# Revit family: ASH_Waste_Multiproduct_BIM_GB_S8735;S8737;S8803;S8808
name_source: partatom
category: Plumbing Fixtures
revit_build: Autodesk Revit MEP 2014 (Build: 20130308_1515(x64)
units: mm (PartAtom-declared; Revit-internal decimal feet)

## types (4) — shared parameters
Accessories = www.idealspec.co.uk
AreaUnits = millimeters
Assembly Code = C1030200
AssetType = Fixed
Brand = Armitage Shanks
BrassMtl = ISI_IdealStandard_Washbasin_Brass_Render
ChromeMtl = ISI_IdealStandard_Washbasin_Chrome_Render
Color = Chrome
ConnectionType = Plumbing
DrainSize = 32 mm
DurationUnit = year
ECA = No
ExpectedLife = 30
Finish = Chrome
Help = www.idealspec.co.uk/contact-us.html
IfcExportAs = IfcWasteTerminalType
IfcExportType = WASTETRAP
InstallationInstructions = www.idealspec.co.uk/resources.html
LinearUnits = millimeters
ManufacturerURL = www.idealspec.co.uk
Material = Brass
NBSDescription = Wastes for wash basins
NBSReference = 45-35-70/372
NettWeight = 0.62 Kg
NominalHeight = 62 mm
NominalWidth = 62 mm
RubberMtl = ISI_IdealStandard_Washbasin_Rubber_Render
Shape = Sculptured
Space = Internal
URL = www.idealspec.co.uk
Uniclass2015Description = Waste traps
Uniclass2015Reference = Pr_65_52_25_98
Uniclass2015Version = Products v1.1
Version = 1
VolumeUnits = Litres
WRAS = No
WarrantyDescription = Manufacturers Warranty
WarrantyDurationParts = 5
WarrantyDurationUnit = year
WashHandBasinMounting = Other
WashHandBasinType = Hand Rinse
WaterEfficientProduct = No
zero-valued in all types: CWFU, Cost, Default Elevation, HWFU, WFU

## per-type parameters (varying)
| type | BIMObjectName | ClickPlug | Description | Features | Model | ModelNumber | ModelReference | Name | NominalDepth | NominalLength | ProductInformation | RubberPlug | Size |
| S8735AA - Waste 1¼" Anti Theft - Bolt & Chain - Slotted - Brass | ISI_IdealStandard_Waste_1¼"AntiTheftBolt&ChainSlotted_S8735AA | No | Waste 1¼" Anti Theft - Bolt & Chain - Slotted - Brass | 1¼" Anti Theft - Bolt & Chain - Slotted - Brass | S8735AA | S8735AA | Waste 1¼" Anti Theft - Bolt & Chain - Slotted - Brass | Waste_1¼"AntiTheftBolt&ChainSlotted_S8735AA_IdealStandard | 89 mm  [stored 0.291995 ft] | 89 mm  [stored 0.291995 ft] | www.idealspec.co.uk/assets/datasheet/S8735AA | Yes | 62 x 89 x 62 mm |
| S8737AA - Waste 1¼" Anti Theft - Slotted - Brass | ISI_IdealStandard_Waste_1¼"AntiTheftSlottedBrass_S8737AA | No | Waste 1¼" Anti Theft - Slotted - Brass | 1¼" Anti Theft - Slotted - Brass | S8737AA | S8737AA | Waste 1¼" Anti Theft - Slotted - Brass | Waste_1¼"AntiTheftSlottedBrass_S8737AA_IdealStandard | 89 mm  [stored 0.291995 ft] | 89 mm  [stored 0.291995 ft] | www.idealspec.co.uk/assets/datasheet/S8737AA | Yes | 62 x 89 x 62 mm |
| S8803AA - Waste 1¼" Click Plug - Slotted - Brass | ISI_IdealStandard_Waste_1¼"ClickPlugSlottedBrass_S8803AA | Yes | Waste 1¼" Click Plug - Slotted - Brass | 1¼" Click Plug - Slotted - Brass | S8803AA | S8803AA | Waste 1¼" Click Plug - Slotted - Brass | Waste_1¼"ClickPlugSlottedBrass_S8803AA_IdealStandard | 84 mm | 84 mm | www.idealspec.co.uk/assets/datasheet/S8803AA | No | 62 x 84 x 62 mm |
| S8808AA - Waste 1¼" Click Plug - Unslotted - Brass | ISI_IdealStandard_Waste_1¼"ClickPlugUnslottedBrass_S8808AA | Yes | Waste 1¼" Click Plug - Unslotted - Brass | 1¼" Click Plug - Unslotted - Brass | S8808AA | S8808AA | Waste 1¼" Click Plug - Unslotted - Brass | Waste_1¼"ClickPlugUnslottedBrass_S8808AA_IdealStandard | 84 mm | 84 mm | www.idealspec.co.uk/assets/datasheet/S8808AA | No | 62 x 84 x 62 mm |

note: [stored X ft] marks values corroborated as IEEE doubles in the binary element streams (Revit-internal decimal feet)

## geometry (parser evidence)
native form markers: Sweep x3
no freeform markers — native parametric forms only
